# Revit family: IHLS-L-254-820-840-x
name_source: partatom
category: Oprawy oświetleniowe
revit_build: Autodesk Revit 2017 (Build: 20190508_0315(x64)
units: mm (PartAtom-declared; Revit-internal decimal feet)

## family parameters
Numer OmniClass = 23.80.70.11
Obiekt nadrzędny = Powierzchnia
Punkt obliczania pomieszczeń = Nie
Tnij formami wycięć po wczytaniu = Nie
Typ części = Normalny
Tytuł OmniClass = Luminaries for Internal Lighting
Współdzielony = Nie
Wymiar okrągłego złącza = Użyj średnicy
Źródło światła = Tak

## types (8) — shared parameters
Emituj kształt widoczny w renderingu = Nie
Emituj z długości prostokąta = 221 mm  [stored 0.725066 ft]
Emituj z szerokości prostokąta = 1174 mm  [stored 3.85171 ft]
Filtr koloru = 16777215
Kod zespołu = D5020200
Lampa = LED
Obciążenie pozorne = 76 VA
Odchylenie kierunku = 90.00°
Producent = RIDI Leuchten GmbH
URL = www.ridi.de
Zmiana temperatury barwowej przyciemniania lampy = <Brak>
brand = RIDI
conformity mark = CE
electrical safety class = 1
height = 80 mm  [stored 0.262467 ft]
ingress protection (IP) code = IP64
length = 1200 mm
nominal frequency = 50-60Hz
nominal voltage = 230
rated input power = 76
voltage type (AC, DC, UC) = AC
width = 248 mm  [stored 0.813648 ft]
zero-valued in all types: Domyślna rzędna

## per-type parameters (varying)
| type | Model | Plik sieci fotometrycznej | weight |
| IHLS-L 254-820-840 SM | 0650555 | IHLS-L 2801260-840 SM.IES | 11.9 kg |
| IHLS-L 254-820-840 SM-DA | 0660555 | IHLS-L 2801260-840 SM.IES | 11.9 kg |
| IHLS-L 254-820-840 SB | 0650079 | IHLS-L-2801260-840 SB.IES | 11.1 kg |
| IHLS-L 254-820-840 SB-DA | 0660079 | IHLS-L-2801260-840 SB.IES | 11.1 kg |
| IHLS-L 254-820-840 OS | 0650089 | IHLS-L 2801240-840 OS.IES | 11.1 kg |
| IHLS-L 254-820-840 OS-DA | 0660089 | IHLS-L 2801240-840 OS.IES | 11.1 kg |
| IHLS-L 254-820-840 W | 0650069 | IHLS-L 2801260-840 W.IES | 11.9 kg |
| IHLS-L 254-820-840 W-DA | 0660069 | IHLS-L 2801260-840 W.IES | 11.9 kg |

note: column(s) folded — value = type name in every type: product name

note: [stored X ft] marks values corroborated as IEEE doubles in the binary element streams (Revit-internal decimal feet)
